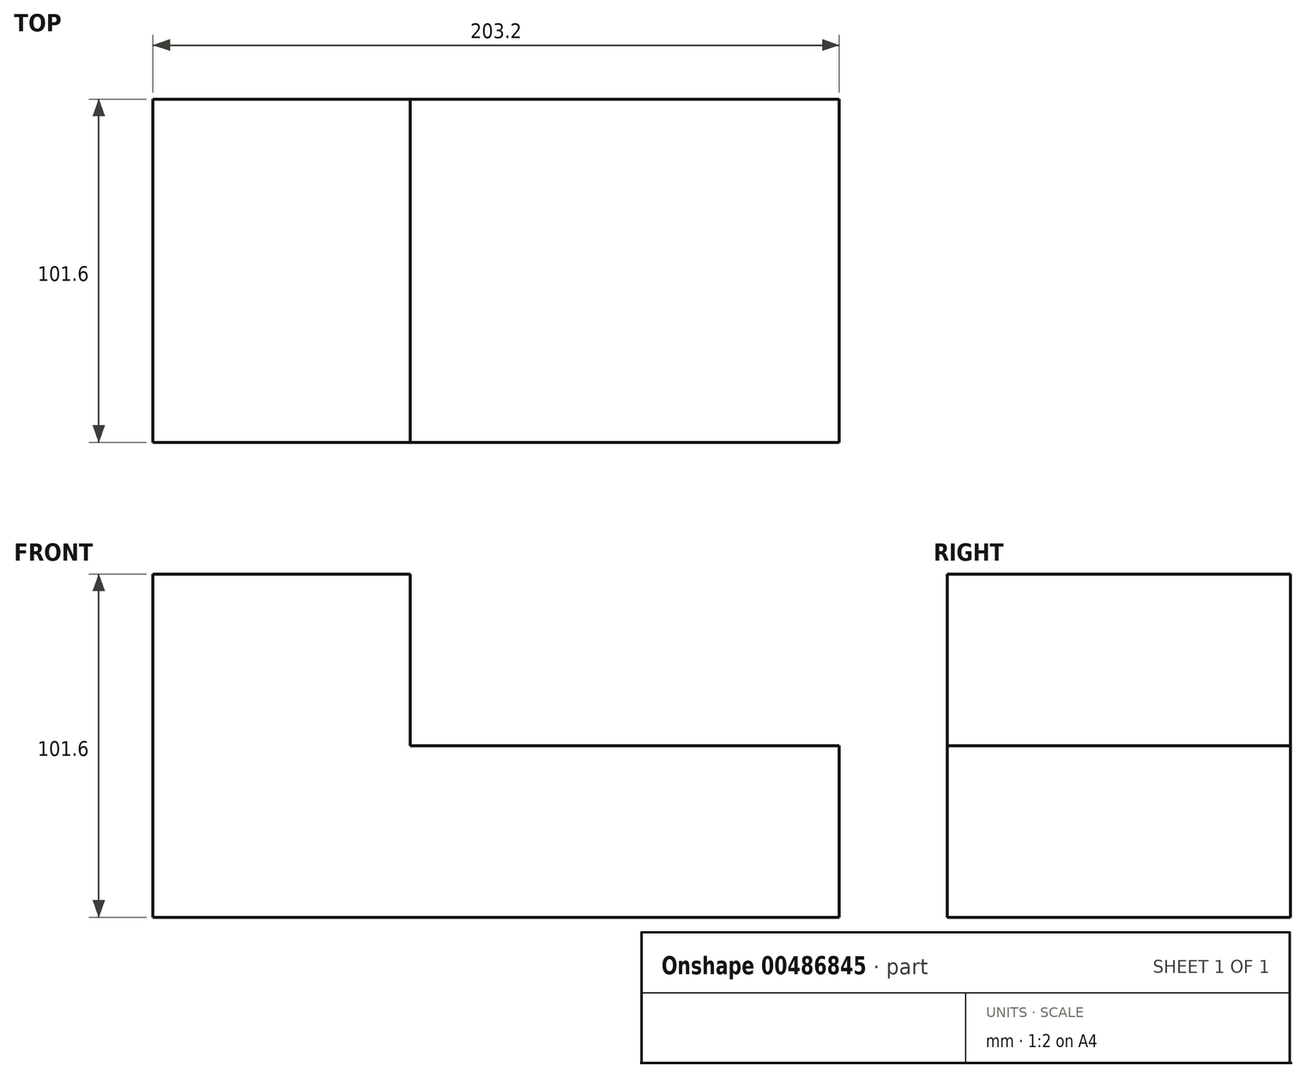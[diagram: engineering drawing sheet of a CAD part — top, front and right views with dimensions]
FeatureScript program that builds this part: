
annotation { "Feature Type Name" : "Feature", "Feature Type Description" : "" }
export const myFeature = defineFeature(function(context is Context, id is Id, definition is map)
    precondition{}
    {
        {
            var Q0;
            Q0=qCreatedBy(makeId("Front.planeOp"),FACE);
            var sketch = newSketch(context, id + "F0", { "sketchPlane" : qUnion([Q0])});
            skLineSegment(sketch, "E0.bottom", {"start": v(0, 0) * mm, "end": v(-203.2, 0) * mm});
            skLineSegment(sketch, "E0.top", {"start": v(-127, 101.6) * mm, "end": v(-203.2, 101.6) * mm});
            skLineSegment(sketch, "E0.left", {"start": v(0, 0) * mm, "end": v(0, 50.8) * mm});
            skLineSegment(sketch, "E0.right", {"start": v(-203.2, 0) * mm, "end": v(-203.2, 101.6) * mm});
            skPoint(sketch, "E1.oppositeSnap0", {"position": v(0, 50.8) * mm});
            skLineSegment(sketch, "E1.bottom", {"start": v(0, 0) * mm, "end": v(-127, 0) * mm});
            skLineSegment(sketch, "E2.top", {"start": v(0, 50.8) * mm, "end": v(-127, 50.8) * mm});
            skLineSegment(sketch, "E2.right", {"start": v(-127, 101.6) * mm, "end": v(-127, 50.8) * mm});
            skPoint(sketch, "E3.orphan", {"position": v(0, 101.6) * mm});
            skSolve(sketch);
        }
        {
            var Q0;
            Q0 = qSketchRegion(id + "F0", true);
            extrude(context, id + "F1", {"entities" : qUnion([Q0]), "depth" : 101.6 * mm});
        }
    });
